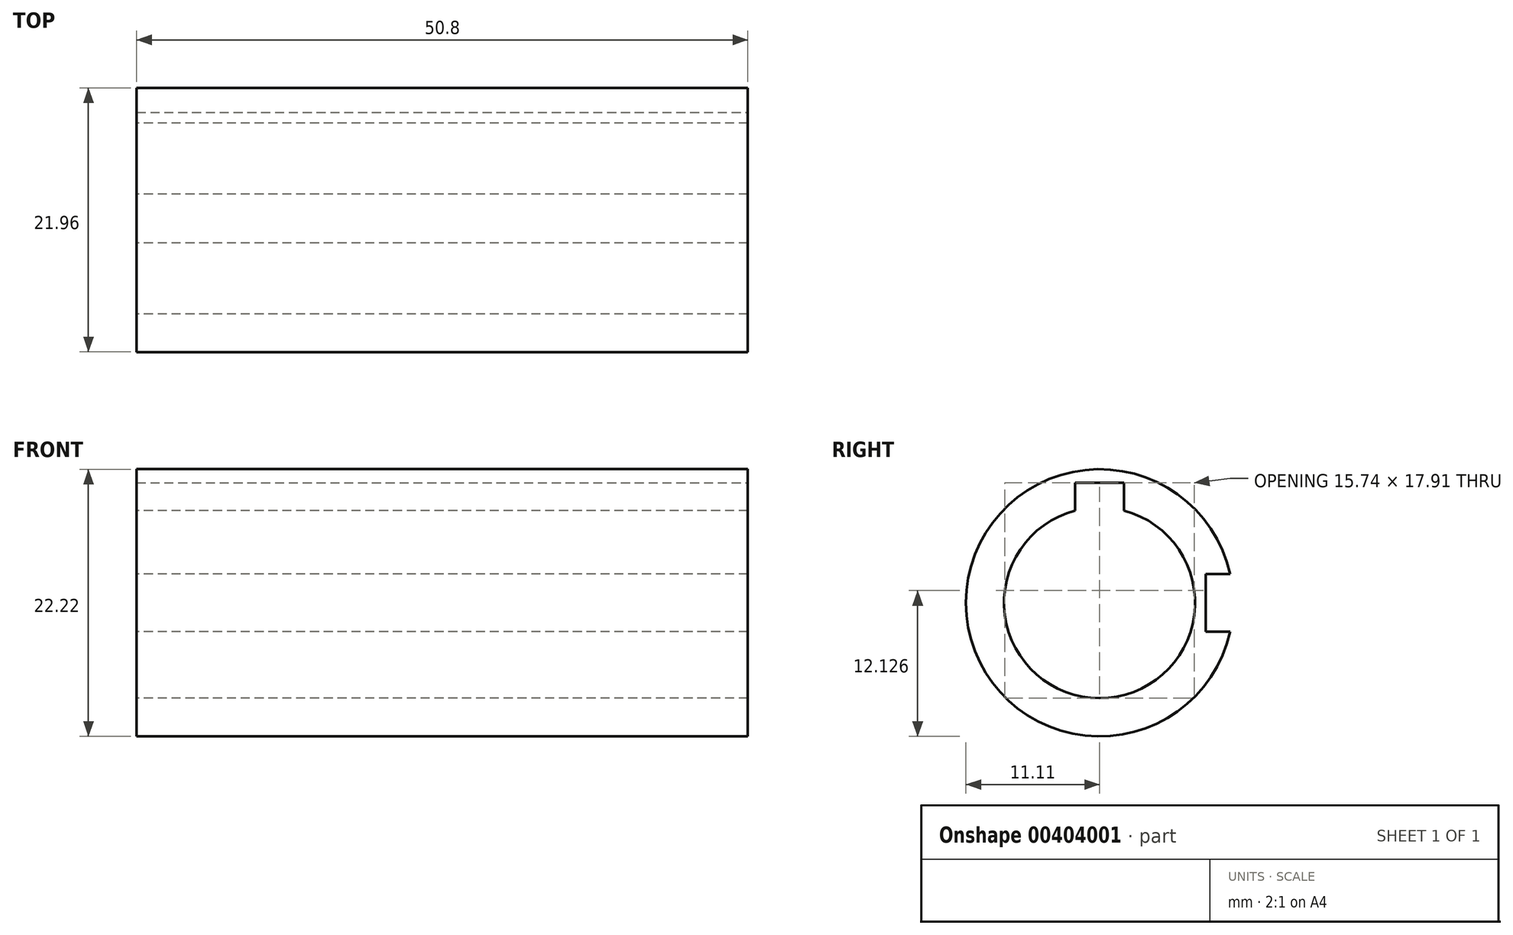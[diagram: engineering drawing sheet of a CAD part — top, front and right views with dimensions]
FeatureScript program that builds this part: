
annotation { "Feature Type Name" : "Feature", "Feature Type Description" : "" }
export const myFeature = defineFeature(function(context is Context, id is Id, definition is map)
    precondition{}
    {
        {
            var Q0;
            Q0=qCreatedBy(makeId("Front.planeOp"),FACE);
            var sketch = newSketch(context, id + "F0", { "sketchPlane" : qUnion([Q0])});
            skLineSegment(sketch, "E0", {"start": v(0, 7.94) * mm, "end": v(50.8, 7.94) * mm});
            skLineSegment(sketch, "E1", {"start": v(0, 7.94) * mm, "end": v(0, 11.11) * mm});
            skLineSegment(sketch, "E2", {"start": v(0, 11.11) * mm, "end": v(50.8, 11.11) * mm});
            skLineSegment(sketch, "E3", {"start": v(50.8, 11.11) * mm, "end": v(50.8, 7.94) * mm});
            skLineSegment(sketch, "E4", {"start": v(0, 0) * mm, "end": v(50.8, 0) * mm, "construction": true});
            skSolve(sketch);
        }
        {
            var Q0;
            Q0 = qSketchRegion(id + "F0", true);
            var Q1;
            Q1=sQuery(id+"F0.wireOp",EDGE,"E4");
            revolve(context, id + "F1", {"entities" : qUnion([Q0]), "axis" : qUnion([Q1]), "revolveType" : RevolveType.FULL});
        }
        {
            var Q0;
            Q0=makeQuery(id+"F1.opRevolve","SWEPT_FACE",FACE,{"disambiguationData":[OSD([sQuery(id+"F0.wireOp",EDGE,"E3")])]});
            var sketch = newSketch(context, id + "F2", { "sketchPlane" : qUnion([Q0])});
            skLineSegment(sketch, "E5.0", {"start": v(-2.03, 9.97) * mm, "end": v(2.03, 9.97) * mm});
            skLineSegment(sketch, "E6.0", {"start": v(-2.03, 7.43) * mm, "end": v(2.03, 7.43) * mm});
            skLineSegment(sketch, "E7", {"start": v(-2.03, 9.97) * mm, "end": v(-2.03, 7.43) * mm});
            skLineSegment(sketch, "E8", {"start": v(2.03, 7.43) * mm, "end": v(2.03, 9.97) * mm});
            skSolve(sketch);
        }
        {
            var Q0;
            Q0 = qSketchRegion(id + "F2", true);
            extrude(context, id + "F3", {"entities" : qUnion([Q0]), "operationType" : NewBodyOperationType.REMOVE, "endBound" : BoundingType.THROUGH_ALL, "oppositeDirection" : true, "depth" : 25.4 * mm});
        }
        {
            var Q0;
            Q0=makeQuery(id+"F1.opRevolve","SWEPT_FACE",FACE,{"disambiguationData":[OSD([sQuery(id+"F0.wireOp",EDGE,"E3")])]});
            var sketch = newSketch(context, id + "F4", { "sketchPlane" : qUnion([Q0])});
            skLineSegment(sketch, "E9.direction1", {"start": v(11.11, 0) * mm, "end": v(8.83, 0) * mm, "construction": true});
            skLineSegment(sketch, "E10", {"start": v(8.83, 2.39) * mm, "end": v(8.83, -2.39) * mm});
            skLineSegment(sketch, "E11", {"start": v(8.83, 2.39) * mm, "end": v(11.11, 2.39) * mm});
            skLineSegment(sketch, "E12", {"start": v(11.11, 2.39) * mm, "end": v(11.11, -2.39) * mm});
            skLineSegment(sketch, "E13", {"start": v(11.11, -2.39) * mm, "end": v(8.83, -2.39) * mm});
            skSolve(sketch);
        }
        {
            var Q0;
            Q0 = qSketchRegion(id + "F4", true);
            extrude(context, id + "F5", {"entities" : qUnion([Q0]), "operationType" : NewBodyOperationType.REMOVE, "endBound" : BoundingType.THROUGH_ALL, "oppositeDirection" : true, "depth" : 25.4 * mm});
        }
    });
